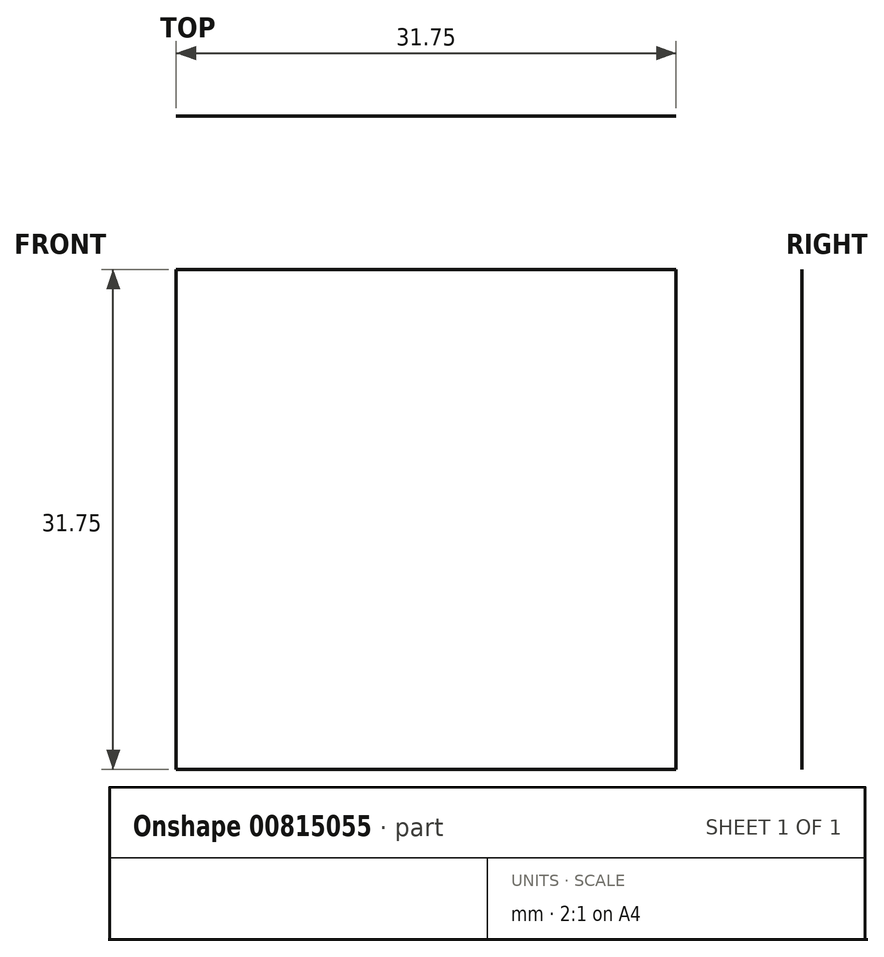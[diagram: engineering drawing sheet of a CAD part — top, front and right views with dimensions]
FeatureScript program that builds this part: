
annotation { "Feature Type Name" : "Feature", "Feature Type Description" : "" }
export const myFeature = defineFeature(function(context is Context, id is Id, definition is map)
    precondition{}
    {
        {
            var Q0;
            Q0=qCreatedBy(makeId("Top.planeOp"),FACE);
            var sketch = newSketch(context, id + "F0", { "sketchPlane" : qUnion([Q0])});
            skLineSegment(sketch, "E0.bottom", {"start": v(0, 0) * mm, "end": v(31.75, 0) * mm});
            skLineSegment(sketch, "E0.top", {"start": v(0, 14.42) * mm, "end": v(31.75, 14.42) * mm});
            skLineSegment(sketch, "E0.left", {"start": v(0, 0) * mm, "end": v(0, 14.42) * mm});
            skLineSegment(sketch, "E0.right", {"start": v(31.75, 0) * mm, "end": v(31.75, 14.42) * mm});
            skSolve(sketch);
        }
        {
            var Q0;
            Q0=sQuery(id+"F0.wireOp",EDGE,"E0.bottom");
            extrude(context, id + "F1", {"bodyType" : ToolBodyType.SURFACE, "surfaceEntities" : qUnion([Q0]), "depth" : 31.75 * mm, "offsetDistance" : 25.4 * mm});
        }
    });
